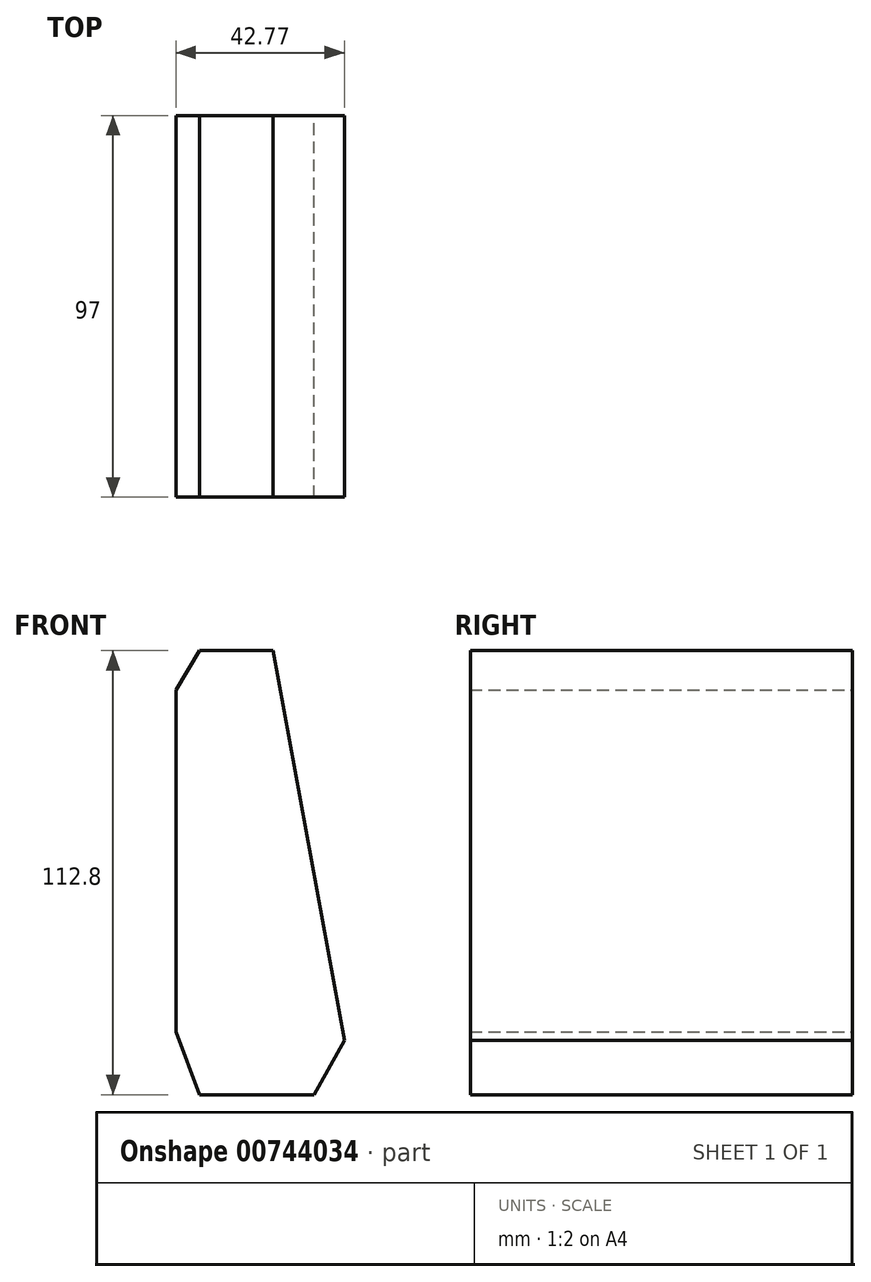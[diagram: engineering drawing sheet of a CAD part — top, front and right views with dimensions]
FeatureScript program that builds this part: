
annotation { "Feature Type Name" : "Feature", "Feature Type Description" : "" }
export const myFeature = defineFeature(function(context is Context, id is Id, definition is map)
    precondition{}
    {
        {
            var Q0;
            Q0=qCreatedBy(makeId("Front.planeOp"),FACE);
            var sketch = newSketch(context, id + "F0", { "sketchPlane" : qUnion([Q0])});
            skLineSegment(sketch, "E0", {"start": v(0, 0) * mm, "end": v(29, 0) * mm});
            skLineSegment(sketch, "E1", {"start": v(29, 0) * mm, "end": v(36.77, 13.8) * mm});
            skLineSegment(sketch, "E2", {"start": v(36.77, 13.8) * mm, "end": v(18.67, 112.8) * mm});
            skLineSegment(sketch, "E3", {"start": v(18.67, 112.8) * mm, "end": v(0, 112.8) * mm});
            skLineSegment(sketch, "E4", {"start": v(-6, 16) * mm, "end": v(0, 0) * mm});
            skLineSegment(sketch, "E5", {"start": v(-6, 16) * mm, "end": v(-6, 102.8) * mm});
            skLineSegment(sketch, "E6", {"start": v(-6, 102.8) * mm, "end": v(0, 112.8) * mm});
            skSolve(sketch);
        }
        {
            var Q0;
            Q0=makeQuery(id+"F0.imprint","IMPRINT",FACE,{"disambiguationData":[TD([[makeQuery(id+"F0.imprint","IMPRINT",EDGE,{"derivedFrom":sQuery(id+"F0.wireOp",EDGE,"E0")}),1.0]])]});
            extrude(context, id + "F1", {"entities" : qUnion([Q0]), "depth" : 97 * mm, "offsetDistance" : 25 * mm});
        }
    });
